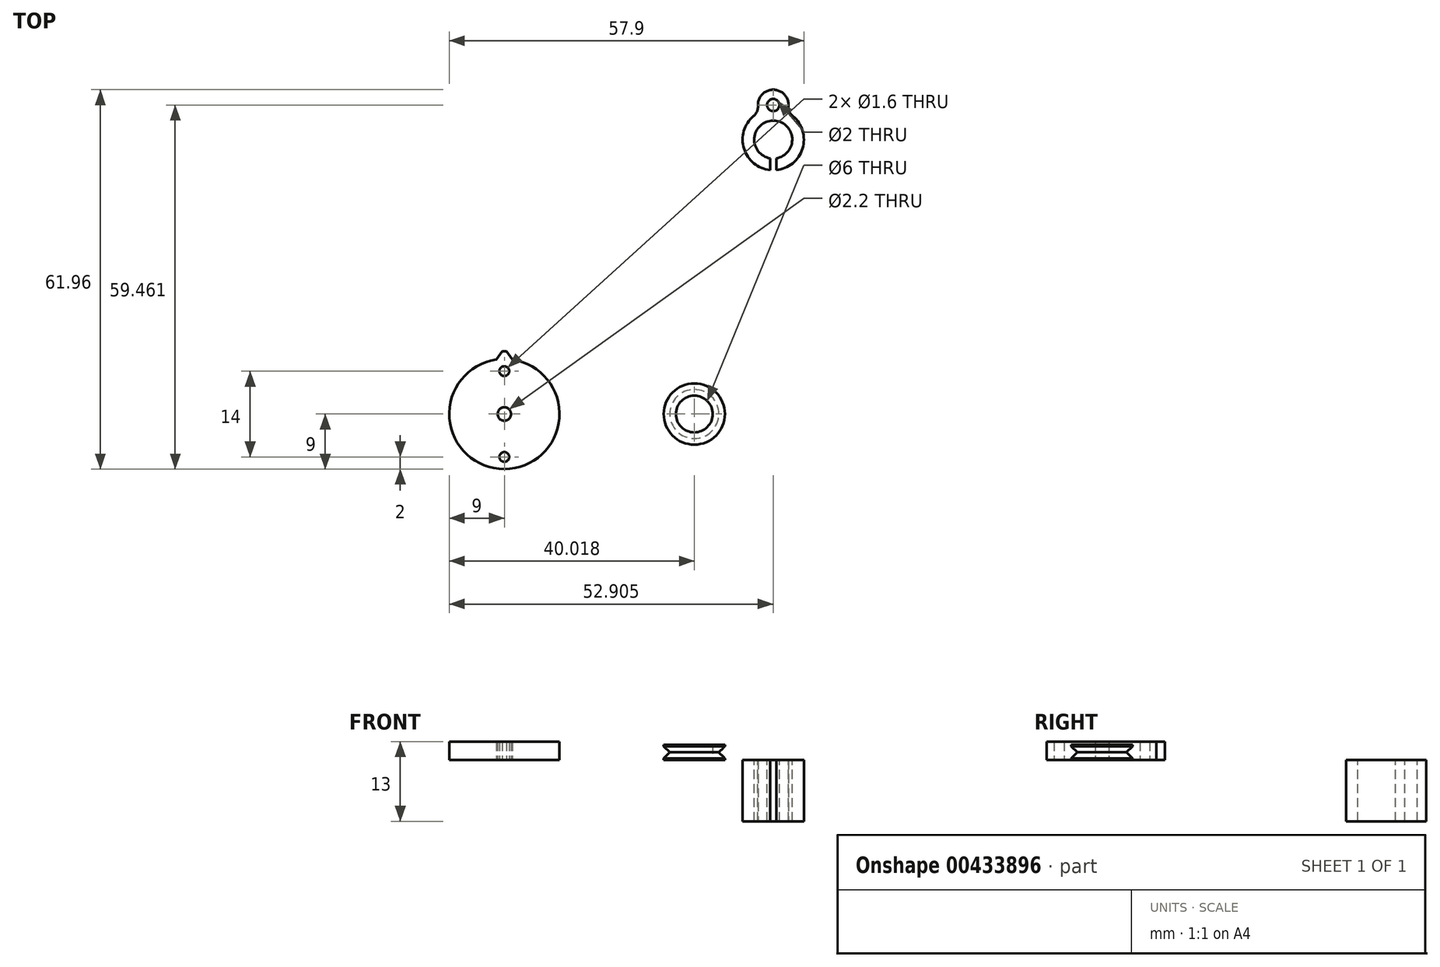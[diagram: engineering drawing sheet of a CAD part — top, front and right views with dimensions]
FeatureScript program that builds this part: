
annotation { "Feature Type Name" : "Feature", "Feature Type Description" : "" }
export const myFeature = defineFeature(function(context is Context, id is Id, definition is map)
    precondition{}
    {
        {
            var Q0;
            Q0=qCreatedBy(makeId("Top.planeOp"),FACE);
            var sketch = newSketch(context, id + "F0", { "sketchPlane" : qUnion([Q0])});
            skCircle(sketch, "E0", {"center": v(0, 0) * mm, "radius": 1.1 * mm});
            skCircle(sketch, "E1", {"center": v(0, 0) * mm, "radius": 9 * mm});
            skSolve(sketch);
        }
        {
            var Q0;
            Q0=makeQuery(id+"F0.imprint","IMPRINT",FACE,{"disambiguationData":[TD([[makeQuery(id+"F0.imprint","IMPRINT",EDGE,{"derivedFrom":sQuery(id+"F0.wireOp",EDGE,"E0")}),-1.0]])]});
            var Q1;
            {var subQ0=sQuery(id+"F0.wireOp",EDGE,"4fpsWwhh-tPYK-AFT6-QJJ7-jzDANFncmwr9");Q1=makeQuery(id+"F0.imprint","IMPRINT",FACE,{"disambiguationData":[TD([[makeQuery(id+"F0.imprint","IMPRINT",EDGE,{"derivedFrom":subQ0}),-1.0]])]});}
            extrude(context, id + "F1", {"entities" : qUnion([Q0, Q1]), "depth" : 3 * mm, "offsetDistance" : 25 * mm});
        }
        {
            var Q0;
            Q0=qCreatedBy(makeId("Top.planeOp"),FACE);
            var sketch = newSketch(context, id + "F2", { "sketchPlane" : qUnion([Q0])});
            skCircle(sketch, "E2", {"center": v(31.02, 0) * mm, "radius": 3 * mm});
            skCircle(sketch, "E3", {"center": v(31.02, 0) * mm, "radius": 5 * mm});
            skSolve(sketch);
        }
        {
            var Q0;
            Q0=makeQuery(id+"F2.imprint","IMPRINT",FACE,{"disambiguationData":[TD([[makeQuery(id+"F2.imprint","IMPRINT",EDGE,{"derivedFrom":sQuery(id+"F2.wireOp",EDGE,"E2")}),-1.0]])]});
            extrude(context, id + "F3", {"entities" : qUnion([Q0]), "depth" : 2.5 * mm, "offsetDistance" : 25 * mm});
        }
        {
            var Q0;
            Q0=qCreatedBy(makeId("Top.planeOp"),FACE);
            var sketch = newSketch(context, id + "F4", { "sketchPlane" : qUnion([Q0])});
            skCircle(sketch, "E4", {"center": v(0, 9) * mm, "radius": 1.3 * mm});
            skCircle(sketch, "E5.0", {"center": v(0, 0) * mm, "radius": 9 * mm});
            skLineSegment(sketch, "E6", {"start": v(-1.3, 8.9) * mm, "end": v(1.3, 8.9) * mm});
            skLineSegment(sketch, "E7", {"start": v(1.3, 8.9) * mm, "end": v(0.33, 10.26) * mm});
            skLineSegment(sketch, "E8", {"start": v(0.33, 10.26) * mm, "end": v(-0.33, 10.26) * mm});
            skLineSegment(sketch, "E9", {"start": v(-0.33, 10.26) * mm, "end": v(-1.3, 8.9) * mm});
            skSolve(sketch);
        }
        {
            var Q0;
            {var subQ4=sQuery(id+"F4.wireOp",EDGE,"E7");Q0=makeQuery(id+"F4.imprint","IMPRINT",FACE,{"disambiguationData":[TD([[makeQuery(id+"F4.imprint","IMPRINT",EDGE,{"derivedFrom":subQ4}),1.0]])]});}
            var Q1;
            Q1=makeQuery(id+"F1.opExtrude","CAP_FACE",FACE,{"disambiguationData":[OSD([sQuery(id+"F0.wireOp",EDGE,"E0"),sQuery(id+"F0.wireOp",EDGE,"E1"),sQuery(id+"F0.wireOp",EDGE,"4fpsWwhh-tPYK-AFT6-QJJ7-jzDANFncmwr9")])],"isStart":false});
            extrude(context, id + "F5", {"entities" : qUnion([Q0]), "operationType" : NewBodyOperationType.ADD, "endBound" : BoundingType.UP_TO_SURFACE, "depth" : 25 * mm, "endBoundEntityFace" : qUnion([Q1]), "offsetDistance" : 25 * mm});
        }
        {
            var Q0;
            Q0=qCreatedBy(makeId("Top.planeOp"),FACE);
            var sketch = newSketch(context, id + "F6", { "sketchPlane" : qUnion([Q0])});
            skLineSegment(sketch, "E10", {"start": v(0, 7) * mm, "end": v(0, -7) * mm, "construction": true});
            skCircle(sketch, "E11", {"center": v(0, 7) * mm, "radius": 0.8 * mm});
            skCircle(sketch, "E12", {"center": v(0, -7) * mm, "radius": 0.8 * mm});
            skPoint(sketch, "E13", {"position": v(0, 0) * mm});
            skSolve(sketch);
        }
        {
            var Q0;
            Q0=makeQuery(id+"F6.imprint","IMPRINT",FACE,{"disambiguationData":[TD([[makeQuery(id+"F6.imprint","IMPRINT",EDGE,{"derivedFrom":sQuery(id+"F6.wireOp",EDGE,"E11")}),1.0]])]});
            var Q1;
            Q1=makeQuery(id+"F6.imprint","IMPRINT",FACE,{"disambiguationData":[TD([[makeQuery(id+"F6.imprint","IMPRINT",EDGE,{"derivedFrom":sQuery(id+"F6.wireOp",EDGE,"E12")}),1.0]])]});
            extrude(context, id + "F7", {"entities" : qUnion([Q0, Q1]), "operationType" : NewBodyOperationType.REMOVE, "depth" : 25 * mm, "offsetDistance" : 25 * mm});
        }
        {
            var Q0;
            Q0=makeQuery(id+"F3.opExtrude","CAP_FACE",FACE,{"disambiguationData":[OSD([sQuery(id+"F2.wireOp",EDGE,"E2"),sQuery(id+"F2.wireOp",EDGE,"E3")])],"isStart":false});
            var Q1;
            Q1=makeQuery(id+"F3.opExtrude","CAP_FACE",FACE,{"disambiguationData":[OSD([sQuery(id+"F2.wireOp",EDGE,"E2"),sQuery(id+"F2.wireOp",EDGE,"E3")])],"isStart":true});
            cPlane(context, id + "F8", {"entities" : qUnion([Q0, Q1]), "cplaneType" : CPlaneType.MID_PLANE, "offset" : 25 * mm, "width" : 150 * mm, "height" : 150 * mm});
        }
        {
            var Q0;
            Q0=qCreatedBy(id+"F8.planeOp",FACE);
            var sketch = newSketch(context, id + "F9", { "sketchPlane" : qUnion([Q0])});
            skCircle(sketch, "E14.0", {"center": v(31.02, 0) * mm, "radius": 5 * mm});
            skCircle(sketch, "E15", {"center": v(31.02, 0) * mm, "radius": 4 * mm});
            skSolve(sketch);
        }
        {
            var Q0;
            Q0 = qSketchRegion(id + "F9", true);
            extrude(context, id + "F10", {"entities" : qUnion([Q0]), "operationType" : NewBodyOperationType.REMOVE, "endBound" : BoundingType.SYMMETRIC, "oppositeDirection" : true, "depth" : 1 * mm, "offsetDistance" : 25 * mm});
        }
        {
            var Q0;
            Q0=makeQuery(id+"F10.boolean.opBoolean","COPY",FACE,{"derivedFrom":makeQuery(id+"F10.opExtrude","CAP_FACE",FACE,{"disambiguationData":[OSD([sQuery(id+"F9.wireOp",EDGE,"E14.0"),sQuery(id+"F9.wireOp",EDGE,"E15")])],"isStart":true})});
            var Q1;
            Q1=makeQuery(id+"F10.boolean.opBoolean","COPY",FACE,{"derivedFrom":makeQuery(id+"F10.opExtrude","CAP_FACE",FACE,{"disambiguationData":[OSD([sQuery(id+"F9.wireOp",EDGE,"E14.0"),sQuery(id+"F9.wireOp",EDGE,"E15")])],"isStart":false})});
            chamfer(context, id + "F11", {"entities" : qUnion([Q0, Q1]), "width" : .5 * mm, "tangentPropagation" : true});
        }
        {
            var Q0;
            Q0=qCreatedBy(makeId("Top.planeOp"),FACE);
            var sketch = newSketch(context, id + "F12", { "sketchPlane" : qUnion([Q0])});
            skCircle(sketch, "E16", {"center": v(43.9, 50.46) * mm, "radius": 1 * mm});
            skCircle(sketch, "E17", {"center": v(43.9, 44.82) * mm, "radius": 3.1 * mm});
            skCircle(sketch, "E18", {"center": v(43.9, 44.82) * mm, "radius": 5 * mm});
            skCircle(sketch, "E19", {"center": v(43.9, 50.46) * mm, "radius": 2.5 * mm});
            skLineSegment(sketch, "E20.bottom", {"start": v(43.4, 42.39) * mm, "end": v(44.4, 42.39) * mm});
            skLineSegment(sketch, "E20.top", {"start": v(43.4, 39.67) * mm, "end": v(44.4, 39.67) * mm});
            skLineSegment(sketch, "E20.left", {"start": v(43.4, 42.39) * mm, "end": v(43.4, 39.67) * mm});
            skLineSegment(sketch, "E20.right", {"start": v(44.4, 42.39) * mm, "end": v(44.4, 39.67) * mm});
            skPoint(sketch, "E21", {"position": v(43.9, 42.39) * mm});
            skSolve(sketch);
        }
        {
            var Q0;
            Q0=makeQuery(id+"F12.imprint","IMPRINT",FACE,{"disambiguationData":[TD([[makeQuery(id+"F12.imprint","IMPRINT",EDGE,{"derivedFrom":sQuery(id+"F12.wireOp",EDGE,"E16")}),-1.0]])]});
            var Q1;
            {var subQ0=sQuery(id+"F12.wireOp",EDGE,"E19");var subQ1=sQuery(id+"F12.wireOp",EDGE,"E18");var subQ2=makeQuery(id+"F12.imprint","INTERSECT",VERTEX,{"disambiguationData":[OD(0.0)],"derivedFrom":[subQ1,subQ0]});Q1=makeQuery(id+"F12.imprint","IMPRINT",FACE,{"disambiguationData":[TD([[makeQuery(id+"F12.imprint","IMPRINT",EDGE,{"disambiguationData":[TD([[subQ2,1.0]])],"derivedFrom":subQ1}),1.0]])]});}
            var Q2;
            {var subQ6=sQuery(id+"F12.wireOp",EDGE,"E20.left");var subQ8=sQuery(id+"F12.wireOp",EDGE,"E17");var subQ10=makeQuery(id+"F12.imprint","INTERSECT",VERTEX,{"derivedFrom":[subQ8,subQ6]});Q2=makeQuery(id+"F12.imprint","IMPRINT",FACE,{"disambiguationData":[TD([[makeQuery(id+"F12.imprint","IMPRINT",EDGE,{"disambiguationData":[TD([[subQ10,1.0]])],"derivedFrom":subQ8}),-1.0]])]});}
            extrude(context, id + "F13", {"entities" : qUnion([Q0, Q1, Q2]), "oppositeDirection" : true, "depth" : 10 * mm, "offsetDistance" : 25 * mm});
        }
        {
            var Q0;
            {var subQ0=sQuery(id+"F12.wireOp",EDGE,"E19");var subQ1=sQuery(id+"F12.wireOp",EDGE,"E18");Q0=makeQuery(id+"F13.opExtrude","SWEPT_EDGE",EDGE,{"disambiguationData":[OSD([subQ1,subQ0]),TDD([makeQuery(id+"F12.imprint","INTERSECT",VERTEX,{"disambiguationData":[OD(0.0)],"derivedFrom":[subQ1,subQ0]})])]});}
            var Q1;
            {var subQ0=sQuery(id+"F12.wireOp",EDGE,"E19");var subQ1=sQuery(id+"F12.wireOp",EDGE,"E18");Q1=makeQuery(id+"F13.opExtrude","SWEPT_EDGE",EDGE,{"disambiguationData":[OSD([subQ1,subQ0]),TDD([makeQuery(id+"F12.imprint","INTERSECT",VERTEX,{"disambiguationData":[OD(1.0)],"derivedFrom":[subQ1,subQ0]})])]});}
            fillet(context, id + "F14", {"entities" : qUnion([Q0, Q1]), "radius" : 2 * mm, "tangentPropagation" : true, "allowEdgeOverflow" : false});
        }
    });
